# Revit family: Faucet-Lavatory-KALLISTA-PINNA_PALETTA-P26623
name_source: partatom
category: Plumbing Fixtures
units: mm (PartAtom-declared; Revit-internal decimal feet)

## family parameters
Cut with Voids When Loaded = No
Host = Face
Maintain Annotation Orientation = No
OmniClass Number = 23.31.11.00
Part Type = Normal
Room Calculation Point = No
Round Connector Dimension = Use Diameter
Shared = No

## types (5) — shared parameters
ADA Compliant = No
Assembly Code = D2010
CW Connection = Yes
Cold Water Inlet = Cold Water Inlet
Date Modified = 11/27/2023
Default Elevation = 36"
Description = Pinna Paletta Single Control
Drain Included = Yes
Flow Rate = 1 GPM
HW Connection = Yes
Handle Clearance = 3"
Height = 9 3/8"
Hot Water Inlet = Hot Water Inlet
Length = 5 3/4"
Manufacturer = Kallista Co.
Master Format 2014 = 22 41 39
Master Format 2014 Name = Residential Faucets, Supplies, and Trim
Material = Premium Metal Construction
Pressure = 0.00 psi
Product Name = Pinna Paletta
Spout Reach = 5 3/4"
URL = https://www.kallista.com
Vent Connection = No
Waste Connection = No
Waste Water Outlet = Waste Water Outlet
WaterSense Certified = No
Width = 2 3/8"

## per-type parameters (varying)
| type | Finish | Model | Secondary Material | Type |
| CPH, CP-Chrome | Kallista-Metal-CP-Chrome | P26623-CPH-CP | Kallista-Metal-CPH-Polished_Chrome | 1 |
| BAF, BAF-Brushed French Gold | Kallista-Metal-BAF-Brushed_French_Gold | P26623-BAF-BAF | Kallista-Metal-BAF-Brushed_French_Gold | 2 |
| SNW, SN-Polished Nickel | Kallista-Metal-SN-Polished_Nickel | P26623-SNW-SN | Kallista-Metal-SNW-Polished_Nickel | 3 |
| ULB, ULB-Unlaquered Brass | Kallista-Metal-ULB-Unlaquered_Brass | P24432-ULB-ULB | Kallista-Metal-ULB-Unlaquered_Brass | 4 |
| BNW, BN-Brushed Nickel | Kallista-Metal-BN-Brushed_Nickel | P24432-BNW-BN | Kallista-Metal-BNW-Brushed_Nickel | 5 |

## geometry (parser evidence)
native form markers: Sweep x7
no freeform markers — native parametric forms only
